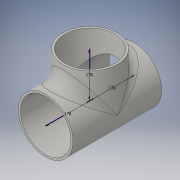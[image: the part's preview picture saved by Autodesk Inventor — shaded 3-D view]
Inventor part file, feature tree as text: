
AUTODESK INVENTOR PART (.ipt)
format: ipt  version: 2016 (Build 200138000, 138)  size: 177,664 bytes
history: native  units: in
note: dims shown in document units (in); Inventor stores cm internally (conversion verified against a paired STEP export)
features: sketch x5, extrude x4, fillet x1
ambient origin geometry x8: Origin, YZ Plane, XZ Plane, XY Plane, X Axis, Y Axis, Z Axis, Center Point
bodies: Solid1 (feature_tree)
feature tree (10):
  sketch  "Sketch1"  dims[d0=7.0079in d1=7.0079in]
  sketch  "Sketch2"  dims[d2=7.0079in d3=8.622in]
  sketch  "Sketch3"  dims[d4=0.322in d5=8.622in]
  extrude  "Extrusion1"  Depth=7.0079in
  extrude  "Extrusion2"  Depth=8.622in
  extrude  "Extrusion3"  Depth=8.622in
  extrude  "Extrusion4"  Depth=14.0157in TaperAngle=0.0deg
  fillet  "Fillet1"  Radius=7.0079in
  sketch  "Sketch4"  dims[d6=0.322in d7=14.0157in d8=0.0in d9=7.0079in d10=0.0in]
  sketch  "Sketch5"  dims[d11=19.685in d12=0.0in d13=7.0079in d14=0.0in d15=1.9685in]
